# Revit family: 3-726-xx - 37-726-xx - Ceres (Outdoor)
name_source: partatom
category: Lighting Fixtures
revit_build: Autodesk Revit 2018 (Build: 20180423_1000(x64)
units: mm (PartAtom-declared; Revit-internal decimal feet)

## family parameters
Cut with Voids When Loaded = No
Host = Face
Light Source = Yes
Part Type = Normal
Room Calculation Point = No
Round Connector Dimension = Use Diameter
Shared = No

## types (2) — shared parameters
Color Filter = 16777215
Diffuser = White Opal Glass
Dimming Lamp Color Temperature Shift = <None>
Emit Shape Visible in Rendering = No
Emit from Circle Diameter = 3 "
Lamp = LED Array
Manufacturer = Oxygen Lighting
Model = 3-726-xx / 37-726-xx - Ceres
Other = <By Category>
Photometric Web File = 3-726-16 Ceres.ies
Tilt Angle = 90.00°
URL = www.oxygenlighting.com
Wattage Comments = 10.30 W at 120 V
zero-valued in all types: Default Elevation

## per-type parameters (varying)
| type | Metal Finish |
| 3-726-16 / 37-726-16 - Ceres | 16 - Gray |
| 3-726-22 / 37-726-22 - Ceres | 22- Oiled Bronze |

## geometry (parser evidence)
native form markers: Sweep x9
no freeform markers — native parametric forms only
